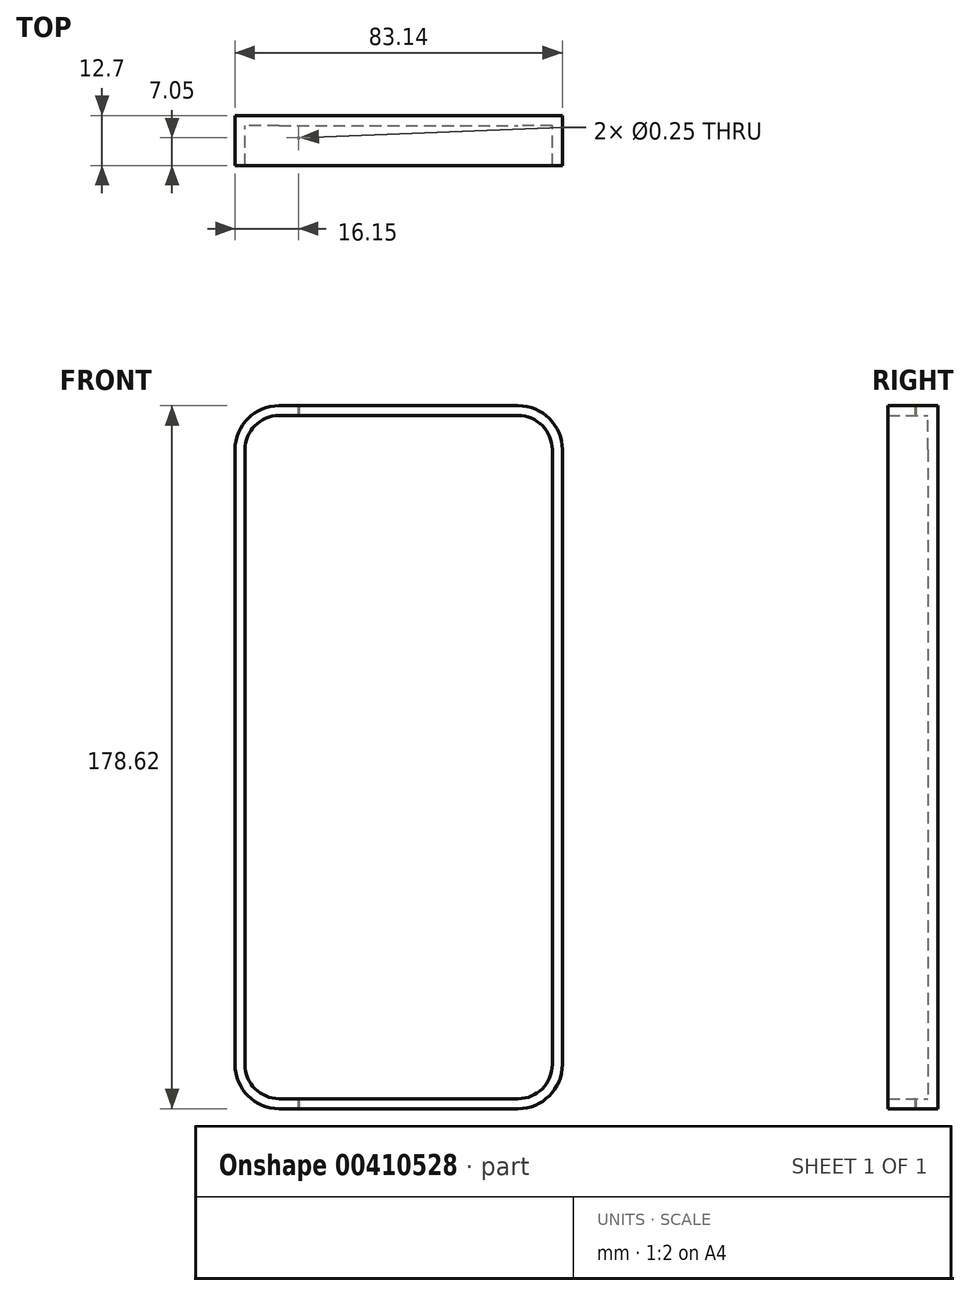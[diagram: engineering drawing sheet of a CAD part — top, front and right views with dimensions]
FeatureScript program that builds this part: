
annotation { "Feature Type Name" : "Feature", "Feature Type Description" : "" }
export const myFeature = defineFeature(function(context is Context, id is Id, definition is map)
    precondition{}
    {
        {
            var Q0;
            Q0=qCreatedBy(makeId("Front.planeOp"),FACE);
            var sketch = newSketch(context, id + "F0", { "sketchPlane" : qUnion([Q0])});
            skLineSegment(sketch, "E0.bottom", {"start": v(-30.2, 96.34) * mm, "end": v(30.53, 96.34) * mm});
            skLineSegment(sketch, "E0.top", {"start": v(-30.2, -82.28) * mm, "end": v(30.53, -82.28) * mm});
            skLineSegment(sketch, "E0.left", {"start": v(-41.4, 85.14) * mm, "end": v(-41.4, -71.08) * mm});
            skLineSegment(sketch, "E0.right", {"start": v(41.74, 85.14) * mm, "end": v(41.74, -71.08) * mm});
            skPoint(sketch, "E1.visualSharp", {"position": v(-41.4, 96.34) * mm});
            skArc(sketch, "E1.filletArc", {"start": v(-30.2, 96.34) * mm, "mid": v(-38.12, 93.06) * mm, "end": v(-41.4, 85.14) * mm});
            skPoint(sketch, "E2.visualSharp", {"position": v(41.74, 96.34) * mm});
            skArc(sketch, "E2.filletArc", {"start": v(41.74, 85.14) * mm, "mid": v(38.45, 93.06) * mm, "end": v(30.53, 96.34) * mm});
            skPoint(sketch, "E3.visualSharp", {"position": v(41.74, -82.28) * mm});
            skArc(sketch, "E3.filletArc", {"start": v(30.53, -82.28) * mm, "mid": v(38.45, -79) * mm, "end": v(41.74, -71.08) * mm});
            skPoint(sketch, "E4.visualSharp", {"position": v(-41.4, -82.28) * mm});
            skArc(sketch, "E4.filletArc", {"start": v(-41.4, -71.08) * mm, "mid": v(-38.12, -79) * mm, "end": v(-30.2, -82.28) * mm});
            skSolve(sketch);
        }
        {
            var Q0;
            Q0 = qSketchRegion(id + "F0", true);
            extrude(context, id + "F1", {"entities" : qUnion([Q0]), "depth" : 12.7 * mm});
        }
        {
            var Q0;
            Q0=makeQuery(id+"F1.opExtrude","CAP_FACE",FACE,{"disambiguationData":[OSD([sQuery(id+"F0.wireOp",EDGE,"E0.bottom"),sQuery(id+"F0.wireOp",EDGE,"E0.top"),sQuery(id+"F0.wireOp",EDGE,"E0.left"),sQuery(id+"F0.wireOp",EDGE,"E0.right"),sQuery(id+"F0.wireOp",EDGE,"E1.filletArc"),sQuery(id+"F0.wireOp",EDGE,"E2.filletArc"),sQuery(id+"F0.wireOp",EDGE,"E3.filletArc"),sQuery(id+"F0.wireOp",EDGE,"E4.filletArc")])],"isStart":false});
            shell(context, id + "F2", {"entities" : qUnion([Q0]), "thickness" : 2.54 * mm});
        }
        {
            var Q0;
            Q0=makeQuery(id+"F1.opExtrude","SWEPT_FACE",FACE,{"disambiguationData":[OSD([sQuery(id+"F0.wireOp",EDGE,"E0.top")])]});
            var sketch = newSketch(context, id + "F3", { "sketchPlane" : qUnion([Q0])});
            skCircle(sketch, "E5", {"center": v(-25.25, 5.65) * mm, "radius": 2.92 * mm});
            skSolve(sketch);
        }
        {
            var Q0;
            Q0=sQuery(id+"F3.wireOp",VERTEX,"E5.center");
            var Q1;
            Q1=makeQuery(id+"F1.opExtrude","SWEPT_BODY",BODY,{"disambiguationData":[OSD([sQuery(id+"F0.wireOp",EDGE,"E0.bottom"),sQuery(id+"F0.wireOp",EDGE,"E0.top"),sQuery(id+"F0.wireOp",EDGE,"E0.left"),sQuery(id+"F0.wireOp",EDGE,"E0.right"),sQuery(id+"F0.wireOp",EDGE,"E1.filletArc"),sQuery(id+"F0.wireOp",EDGE,"E2.filletArc"),sQuery(id+"F0.wireOp",EDGE,"E3.filletArc"),sQuery(id+"F0.wireOp",EDGE,"E4.filletArc")])]});
            hole(context, id + "F4", {"style" : HoleStyle.C_BORE, "endStyle" : HoleEndStyle.THROUGH, "holeDiameter" : 0.25 * mm, "cBoreDiameter" : 12.7 * mm, "cBoreDepth" : 0 * mm, "isTappedThrough" : true, "tappedDepth" : 12.7 * mm, "tapClearance" : 3, "locations" : qUnion([Q0]), "scope" : qUnion([Q1])});
        }
    });
